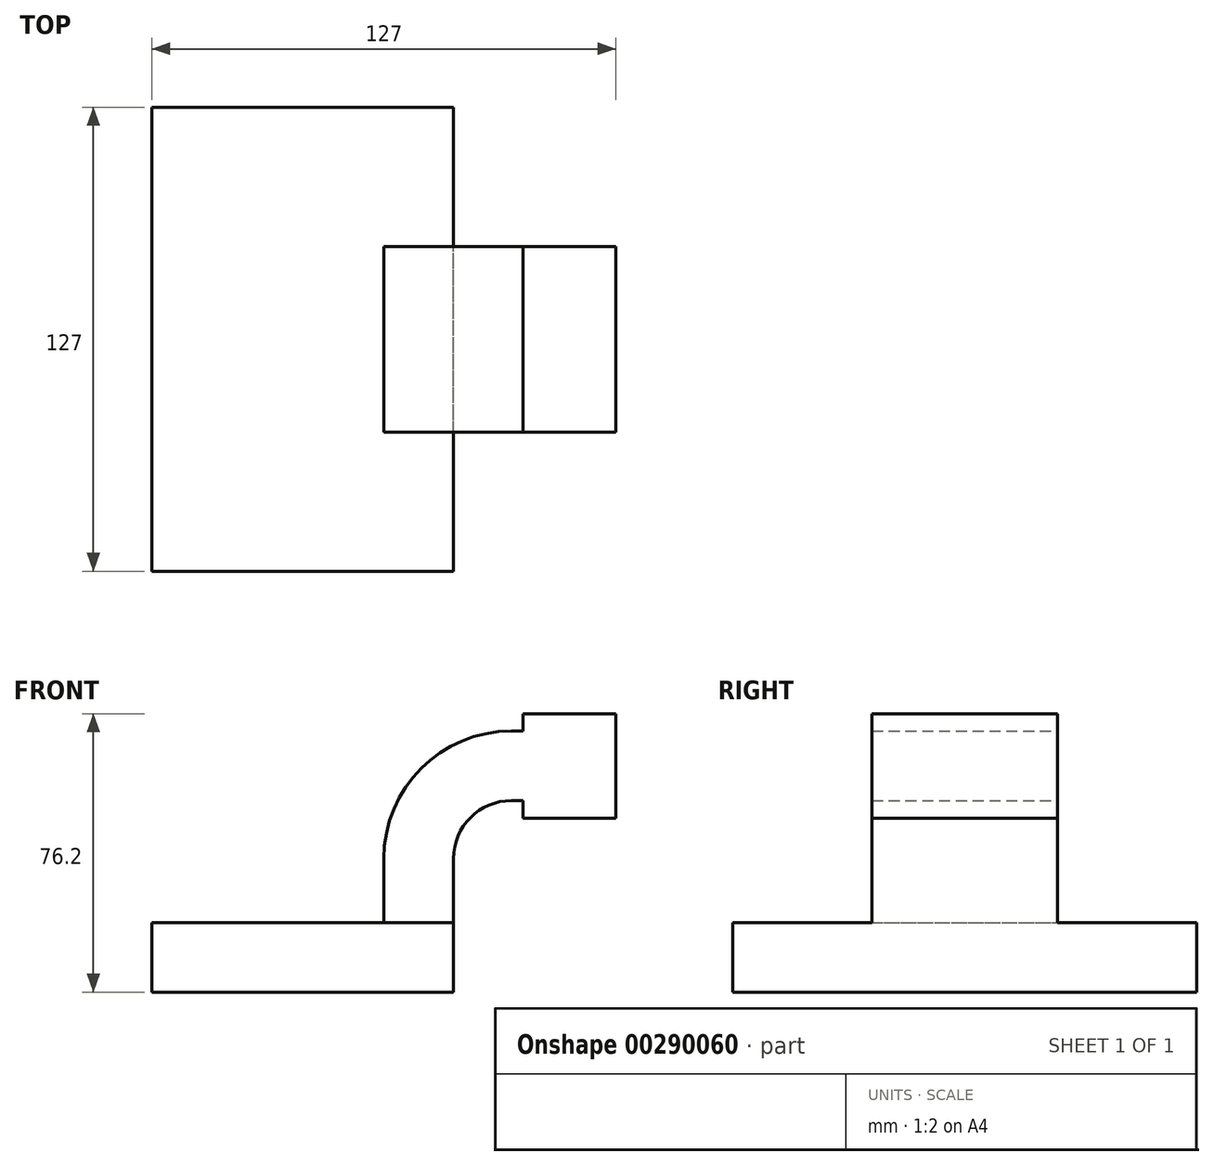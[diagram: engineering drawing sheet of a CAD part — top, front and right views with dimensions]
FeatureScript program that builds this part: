
annotation { "Feature Type Name" : "Feature", "Feature Type Description" : "" }
export const myFeature = defineFeature(function(context is Context, id is Id, definition is map)
    precondition{}
    {
        {
            var Q0;
            Q0=qCreatedBy(makeId("Front.planeOp"),FACE);
            var sketch = newSketch(context, id + "F0", { "sketchPlane" : qUnion([Q0])});
            skLineSegment(sketch, "E0.bottom", {"start": v(41.28, 9.53) * mm, "end": v(-41.28, 9.53) * mm});
            skLineSegment(sketch, "E0.top", {"start": v(41.28, -9.52) * mm, "end": v(-41.28, -9.52) * mm});
            skLineSegment(sketch, "E0.left", {"start": v(41.28, 9.52) * mm, "end": v(41.28, -9.52) * mm});
            skLineSegment(sketch, "E0.right", {"start": v(-41.28, 9.53) * mm, "end": v(-41.28, -9.52) * mm});
            skPoint(sketch, "E0.middle", {"position": v(0, 0) * mm});
            skLineSegment(sketch, "E1.bottom", {"start": v(60.33, 66.68) * mm, "end": v(111.13, 66.68) * mm});
            skLineSegment(sketch, "E1.top", {"start": v(60.33, 38.1) * mm, "end": v(111.13, 38.1) * mm});
            skLineSegment(sketch, "E1.left", {"start": v(60.33, 66.68) * mm, "end": v(60.33, 38.1) * mm});
            skLineSegment(sketch, "E1.right", {"start": v(111.13, 66.68) * mm, "end": v(111.13, 38.1) * mm});
            skPoint(sketch, "E1.middle", {"position": v(85.73, 52.39) * mm});
            skLineSegment(sketch, "E2", {"start": v(41.28, 9.53) * mm, "end": v(41.28, 27) * mm});
            skArc(sketch, "E3", {"start": v(41.28, 27) * mm, "mid": v(45.92, 38.23) * mm, "end": v(57.15, 42.88) * mm});
            skLineSegment(sketch, "E4", {"start": v(57.15, 42.88) * mm, "end": v(85.72, 42.88) * mm});
            skLineSegment(sketch, "E5.0", {"start": v(57.15, 61.93) * mm, "end": v(85.72, 61.93) * mm});
            skArc(sketch, "E5.1", {"start": v(22.23, 27) * mm, "mid": v(32.45, 51.7) * mm, "end": v(57.15, 61.93) * mm});
            skLineSegment(sketch, "E5.2", {"start": v(22.23, 9.53) * mm, "end": v(22.23, 27) * mm});
            skLineSegment(sketch, "E6", {"start": v(85.73, 38.1) * mm, "end": v(85.73, 66.68) * mm});
            skFitSpline(sketch, "E7", {"points": [v(-41.28, 9.52) * mm, v(57.15, 61.93) * mm], "startDerivative": vector(1.21, 93.6) * mm, "endDerivative": vector(189.43, -0.14) * mm});
            skSolve(sketch);
        }
        {
            var Q0;
            Q0=makeQuery(id+"F0.imprint","IMPRINT",FACE,{"disambiguationData":[TD([[makeQuery(id+"F0.imprint","IMPRINT",EDGE,{"derivedFrom":sQuery(id+"F0.wireOp",EDGE,"E0.top")}),-1.0]])]});
            extrude(context, id + "F1", {"entities" : qUnion([Q0]), "endBound" : BoundingType.SYMMETRIC, "depth" : 127 * mm});
        }
        {
            var Q0;
            {var subQ1=sQuery(id+"F0.wireOp",EDGE,"E2");Q0=makeQuery(id+"F0.imprint","IMPRINT",FACE,{"disambiguationData":[TD([[makeQuery(id+"F0.imprint","IMPRINT",EDGE,{"derivedFrom":subQ1}),1.0]])]});}
            var Q1;
            {var subQ0=sQuery(id+"F0.wireOp",EDGE,"E5.0");var subQ1=sQuery(id+"F0.wireOp",EDGE,"E1.left");var subQ2=makeQuery(id+"F0.imprint","INTERSECT",VERTEX,{"derivedFrom":[subQ1,subQ0]});Q1=makeQuery(id+"F0.imprint","IMPRINT",FACE,{"disambiguationData":[TD([[makeQuery(id+"F0.imprint","IMPRINT",EDGE,{"disambiguationData":[TD([[subQ2,-1.0]])],"derivedFrom":subQ1}),1.0]])]});}
            var Q2;
            {var subQ0=sQuery(id+"F0.wireOp",EDGE,"E1.left");var subQ1=sQuery(id+"F0.wireOp",EDGE,"E1.bottom");var subQ2=makeQuery(id+"F0.imprint","INTERSECT",VERTEX,{"derivedFrom":[subQ1,subQ0]});Q2=makeQuery(id+"F0.imprint","IMPRINT",FACE,{"disambiguationData":[TD([[makeQuery(id+"F0.imprint","IMPRINT",EDGE,{"disambiguationData":[TD([[subQ2,-1.0]])],"derivedFrom":subQ1}),-1.0]])]});}
            var Q3;
            {var subQ0=sQuery(id+"F0.wireOp",EDGE,"E1.left");var subQ1=sQuery(id+"F0.wireOp",EDGE,"E1.top");var subQ2=makeQuery(id+"F0.imprint","INTERSECT",VERTEX,{"derivedFrom":[subQ1,subQ0]});Q3=makeQuery(id+"F0.imprint","IMPRINT",FACE,{"disambiguationData":[TD([[makeQuery(id+"F0.imprint","IMPRINT",EDGE,{"disambiguationData":[TD([[subQ2,-1.0]])],"derivedFrom":subQ1}),1.0]])]});}
            extrude(context, id + "F2", {"entities" : qUnion([Q0, Q1, Q2, Q3]), "operationType" : NewBodyOperationType.ADD, "endBound" : BoundingType.SYMMETRIC, "depth" : 50.8 * mm});
        }
        {
            var Q0;
            Q0=makeQuery(id+"F0.imprint","IMPRINT",FACE,{"disambiguationData":[TD([[makeQuery(id+"F0.imprint","IMPRINT",EDGE,{"derivedFrom":sQuery(id+"F0.wireOp",EDGE,"E5.1")}),1.0]])]});
            extrude(context, id + "F3", {"entities" : qUnion([Q0]), "operationType" : NewBodyOperationType.ADD, "endBound" : BoundingType.SYMMETRIC, "depth" : 6.35 * mm});
        }
    });
